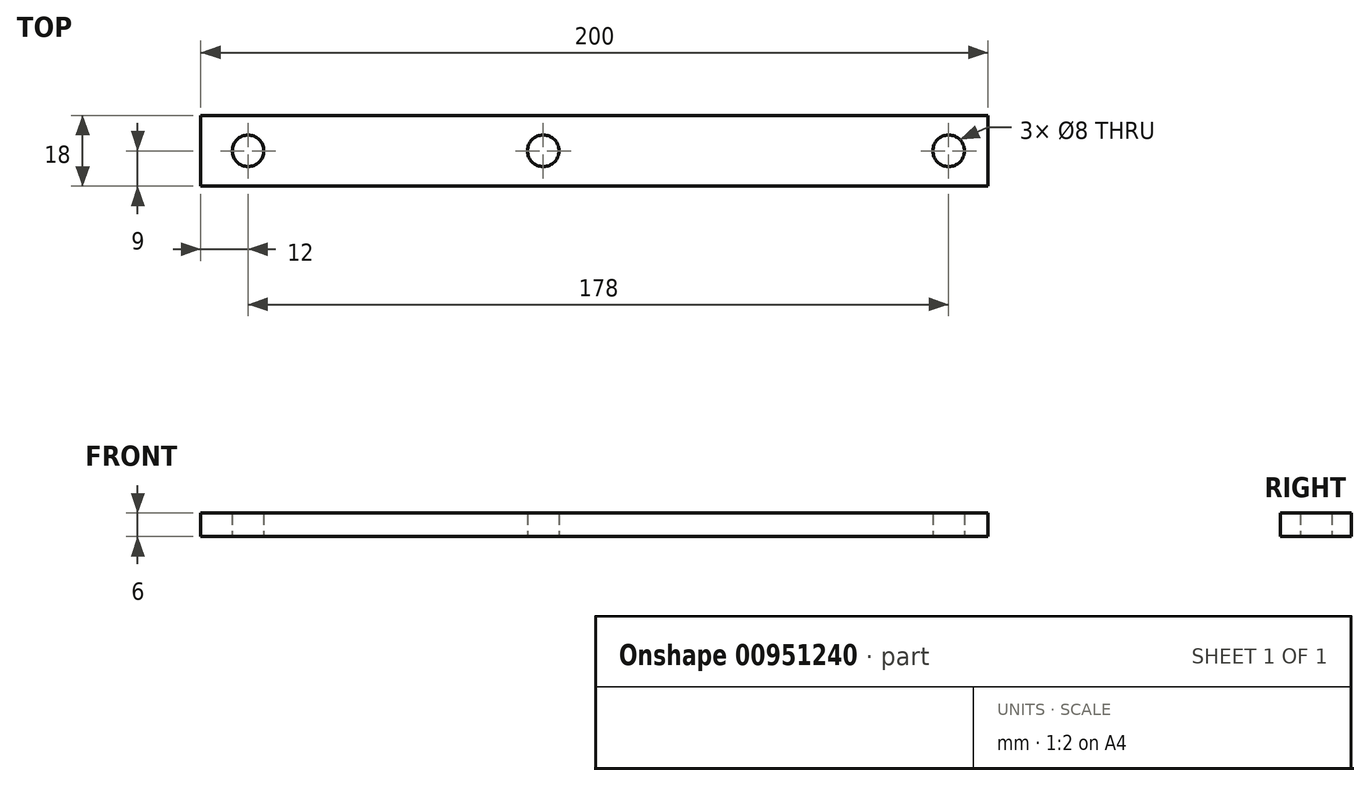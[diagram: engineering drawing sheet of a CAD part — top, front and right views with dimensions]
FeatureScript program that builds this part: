
annotation { "Feature Type Name" : "Feature", "Feature Type Description" : "" }
export const myFeature = defineFeature(function(context is Context, id is Id, definition is map)
    precondition{}
    {
        {
            var Q0;
            Q0=qCreatedBy(makeId("Top.planeOp"),FACE);
            var sketch = newSketch(context, id + "F0", { "sketchPlane" : qUnion([Q0])});
            skLineSegment(sketch, "E0.bottom", {"start": v(0, 0) * mm, "end": v(200, 0) * mm});
            skLineSegment(sketch, "E0.top", {"start": v(0, 18) * mm, "end": v(200, 18) * mm});
            skLineSegment(sketch, "E0.left", {"start": v(0, 0) * mm, "end": v(0, 18) * mm});
            skLineSegment(sketch, "E0.right", {"start": v(200, 0) * mm, "end": v(200, 18) * mm});
            skCircle(sketch, "E1", {"center": v(12, 9) * mm, "radius": 4 * mm});
            skPoint(sketch, "E1.centerSnap0", {"position": v(0, 9) * mm});
            skCircle(sketch, "E2", {"center": v(87, 9) * mm, "radius": 4 * mm});
            skCircle(sketch, "E3", {"center": v(190, 9) * mm, "radius": 4 * mm});
            skPoint(sketch, "E3.centerSnap0", {"position": v(200, 9) * mm});
            skSolve(sketch);
        }
        {
            var Q0;
            Q0=makeQuery(id+"F0.imprint","IMPRINT",FACE,{"disambiguationData":[TD([[makeQuery(id+"F0.imprint","IMPRINT",EDGE,{"derivedFrom":sQuery(id+"F0.wireOp",EDGE,"E0.bottom")}),1.0]])]});
            extrude(context, id + "F1", {"entities" : qUnion([Q0]), "depth" : 6 * mm, "offsetDistance" : 25 * mm});
        }
    });
